# Revit family: DAHD0045_Dolphy_Handdryer
name_source: partatom
category: Mechanical Equipment
units: mm (PartAtom-declared; Revit-internal decimal feet)

## family parameters
Always vertical = Yes
Cut with Voids When Loaded = No
OmniClass Number = 23.75.00.00
OmniClass Title = Climate Control (HVAC)
Part Type = Normal
Room Calculation Point = No
Round Connector Dimension = Use Diameter
Shared = No
Work Plane-Based = No

## types (1)
- DAHD0045_Dolphy_Handdryer
    Default Elevation = 0 mm  [stored 0 ft]
    Depth = 135 mm  [stored 0.442913 ft]
    Description = Airblade Jet Hand Dryer – White
    Hand Dryer Material = High Grade Abs Plastic
    Height = 395 mm  [stored 1.29593 ft]
    Height above floor = Please Refer Spec Sheet at our website.
    Manufacturer = Dolphy Australia
    Material = High Grade ABS Plastic
    Model = DAHD0045
    Product Page Link = https://www.dolphy.com.au
    Tel No. = 1300 605 313
    URL = www.dolphy.com.au
    Voltage = 0 V
    Width = 235 mm  [stored 0.770997 ft]

note: [stored X ft] marks values corroborated as IEEE doubles in the binary element streams (Revit-internal decimal feet)

## geometry (parser evidence)
native form markers: Sweep x3
no freeform markers — native parametric forms only
